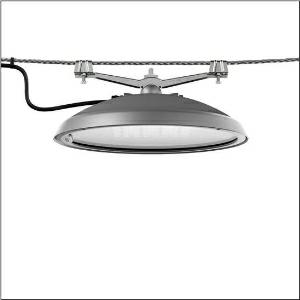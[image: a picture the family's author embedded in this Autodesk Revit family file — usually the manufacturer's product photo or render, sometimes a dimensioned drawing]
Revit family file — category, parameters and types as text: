
# Revit family: dl_50_iq_mini___p1_0s_5xa248u41f08ge_a477
name_source: partatom
category: Lighting Fixtures
units: mm (PartAtom-declared; Revit-internal decimal feet)

## family parameters
Cut with Voids When Loaded = No
Host = Face
Light Source = No
Part Type = Normal
Room Calculation Point = No
Round Connector Dimension = Use Diameter
Shared = No

## types (1)
- --- (1 x LED, 5030 lm, 31.2 W, 4000K)
    Apparent Load = 31 VA
    CIE Flux Codes = 23 54 93 100 100
    Color Rendering = 70
    Color Temperature = 4000K
    Default Elevation = 1800 mm
    Description = DL 50 iQ mini, catenary luminaire, primary light control with lens, of PMMA, primary optical cover: cover, of toughened safety glass, transparent, light distribution: P1.0s, light emission: direct distribution, primary light characteristic: symmetric, installation type: suspended mounting, LED, High Power LED, rated luminous flux: 5.030lm, luminous efficacy: 161lm/W, light colour: 740, colour temperature: 4000K, control gear: iQ Street-Remote, control: optimised constant luminous flux control (CLO 2.0), Desk-Remote (wireless, voltage-free reading and setting of iQ features in the workshop via application-optimized NFC function/RFID function), Light-Fading, Smart-Wire, Night-Set, Lumen-Switch, Temp-Guard, Auto-Match, Street-Remote, mains connection: 230..240V, AC, 50/60Hz, start of lifetime: 31W, end of service life: 32W, reduction: 15W, luminaire housing, of diecast aluminium, powder-coated, SITECO metallic grey (DB 702S), diameter: 500mm, height: 115mm, mounting height: 4..12m, protection rating (complete): IP66, insulation class (complete): insulation class II (safety insulation), certification: CE, ENEC, ENEC+, VDE, impact resistance: IK08, permissible operating ambient temperature for outdoor applications: -25..+40°C, standard-compliant lighting for roads and squares, packaging unit: 1 piece

Light Distribution: P1.0s
    Height = 124 mm
    Lamp = 1 x LED
    Lamp Light Flux = 5030 lm
    Lamp Power = 31.2 W
    Lamp count = 1
    Length = 500 mm
    Luminous efficacy = 161 lm/W
    Manufacturer = Siteco
    ModVariant = No
    Model = 5XA248U41F08GE
    Number of Poles = 1
    OnlyDefault = Yes
    Power Factor = 1
    Product Name = DL 50 iQ mini | P1.0s
    Product group = catenary luminaire
    ProductGroupID = 6300
    Protection Class = Protection class II
    Protection Degree = IP 66
    RLX_Detail_Level = 1
    RLX_Emergency_Light_Flux = 0 lm
    RLX_Emergency_Type = 0
    RLX_Emergency_Type_DB = No
    RlxData = <blob elided: 123477 chars, md5=e8ca0f85>
    Socket = socket
    Standby Power = 0 W
    System Light Flux = 5030 lm
    System Power = 31 W
    Type Comments = factory setting: luminous flux: 100 % | dim-lin: 254 | 325 mA
    Type Image = l_1242791.jpg
    URL = http://relux.com
    VarID = @adj_139679
    Voltage = 0 V
    Weight = 0.00 kg
    Width = 0 mm  [stored 0 ft]

note: [stored X ft] marks values corroborated as IEEE doubles in the binary element streams (Revit-internal decimal feet)

## geometry (parser evidence)
native form markers: Blend x4, Sweep x12
no freeform markers — native parametric forms only
